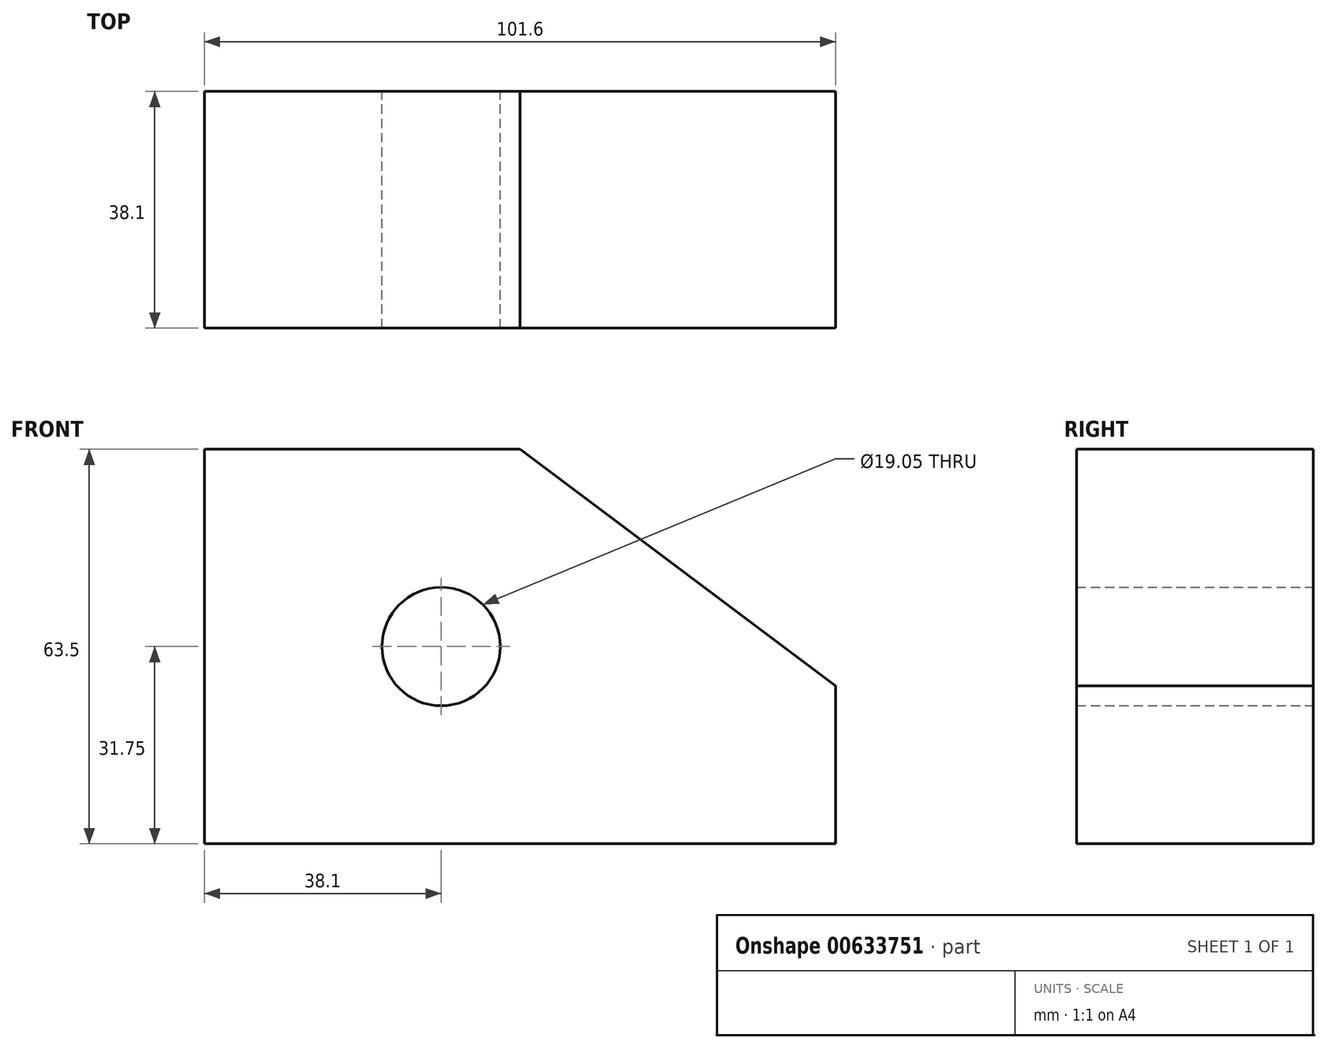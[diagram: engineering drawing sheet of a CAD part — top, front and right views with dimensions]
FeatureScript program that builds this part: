
annotation { "Feature Type Name" : "Feature", "Feature Type Description" : "" }
export const myFeature = defineFeature(function(context is Context, id is Id, definition is map)
    precondition{}
    {
        {
            var Q0;
            Q0=qCreatedBy(makeId("Front.planeOp"),FACE);
            var sketch = newSketch(context, id + "F0", { "sketchPlane" : qUnion([Q0])});
            skLineSegment(sketch, "E0", {"start": v(0, 0) * mm, "end": v(101.6, 0) * mm});
            skLineSegment(sketch, "E1", {"start": v(101.6, 0) * mm, "end": v(101.6, 25.4) * mm});
            skLineSegment(sketch, "E2", {"start": v(0, 0) * mm, "end": v(0, 63.5) * mm});
            skLineSegment(sketch, "E3", {"start": v(0, 63.5) * mm, "end": v(50.8, 63.5) * mm});
            skLineSegment(sketch, "E4", {"start": v(50.8, 63.5) * mm, "end": v(101.6, 25.4) * mm});
            skPoint(sketch, "E5.endSnap0", {"position": v(-6.2, 31.75) * mm});
            skPoint(sketch, "E6.orphan", {"position": v(-12.4, 31.75) * mm});
            skCircle(sketch, "E7", {"center": v(38.1, 31.75) * mm, "radius": 9.53 * mm});
            skPoint(sketch, "E8.orphan", {"position": v(0, 31.75) * mm});
            skSolve(sketch);
        }
        {
            var Q0;
            Q0 = qSketchRegion(id + "F0", true);
            extrude(context, id + "F1", {"entities" : qUnion([Q0]), "depth" : 38.1 * mm, "offsetDistance" : 25.4 * mm});
        }
    });
